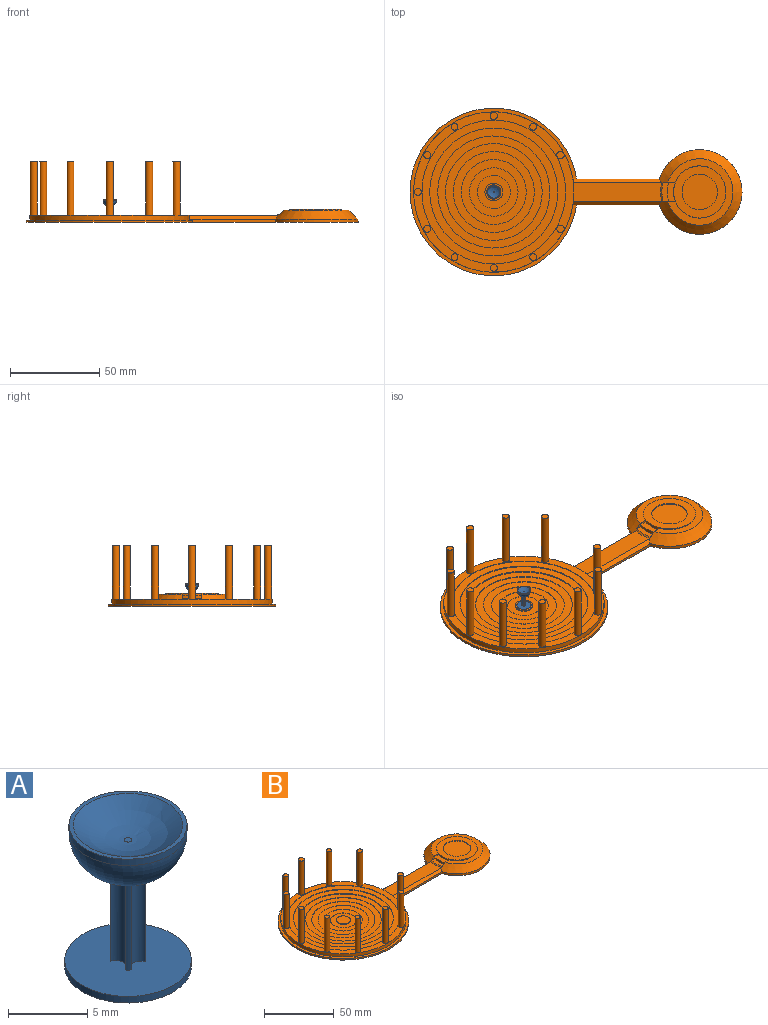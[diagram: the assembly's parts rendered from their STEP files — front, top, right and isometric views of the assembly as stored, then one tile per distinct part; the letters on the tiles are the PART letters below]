
ASSEMBLY  parts=2 mates=1
PART A: 20 faces, bbox 8x8x10.9 mm
  f0: plane 0.8x0.26mm, normal (0,0,-1), area 0.1mm2, adj f7,f17
  f1: plane 0.73x0.22mm, normal (0,0,-1), area 0.1mm2, adj f13,f17
  f2: plane 0.75x0.23mm, normal (0,0,-1), area 0.1mm2, adj f11,f17
  f3: cylinder r=4mm len=8mm, axis (0,0,-1), area 12.8mm2, adj f4,f5
  f4: plane 8x8mm, normal (0,0,1), area 48.8mm2, adj f3,f6,f7,f8,f9,f10,f11,f12
  f5: plane 8x8mm, normal (0,0,-1), area 50.3mm2, adj f3
  f6: cylinder r=1.12mm len=6.89mm, axis (0,0,-1), area 2.4mm2, adj f4,f7,f13,f17
  f7: cylinder r=0.71mm len=6.89mm, axis (0,0,-1), area 12.2mm2, adj f0,f4,f6,f8,f17
  f8: cylinder r=1.12mm len=6.89mm, axis (0,0,-1), area 2.6mm2, adj f4,f7,f9,f17
  f9: cylinder r=0.64mm len=6.89mm, axis (0,0,-1), area 11.2mm2, adj f4,f8,f10,f16,f17
  f10: cylinder r=1.12mm len=6.89mm, axis (0,0,-1), area 2.9mm2, adj f4,f9,f11,f17
  f11: cylinder r=0.68mm len=6.89mm, axis (0,0,-1), area 11.8mm2, adj f2,f4,f10,f12,f17
  f12: cylinder r=1.12mm len=6.89mm, axis (0,0,-1), area 2.6mm2, adj f4,f11,f13,f17
  f13: cylinder r=0.67mm len=6.89mm, axis (0,0,-1), area 11.7mm2, adj f1,f4,f6,f12,f17
  f14: cylinder r=3.73mm len=7.46mm, axis (0,0,-1), area 11.5mm2, adj f15,f17
  f15: plane 7.46x7.46mm, normal (0,0,1), area 6.3mm2, adj f14,f19
  f16: plane 0.66x0.18mm, normal (0,0,-1), area 0.1mm2, adj f9,f17
  f17: torus R=0.66mm, axis (0,0,1), area 78.6mm2, adj f0,f1,f2,f6,f7,f8,f9,f10
  f18: plane 0.48x0.48mm, normal (0,0,1), area 0.2mm2, adj f19
  f19: torus R=0.24mm, axis (0,0,-1), area 41.7mm2, adj f15,f18
PART B: 62 faces, bbox 186.4x94.1x34.1 mm
  f0: cylinder r=14.63mm len=29.27mm, axis (0,0,-1), area 62.7mm2, adj f2,f32,f33,f36,f59
  f1: plane 11.1x3.97mm, normal (0,0,1), area 34.9mm2, adj f2,f32,f34,f35
  f2: plane 6.98x2.59mm, normal (0,-1,0), area 8.5mm2, adj f0,f1,f33,f34,f35,f36
  f3: plane 48.53x1.58mm, normal (0,1,0), area 74.1mm2, adj f5,f25,f28,f29,f30,f31
  f4: plane 48.53x1.58mm, normal (0,-1,0), area 74.1mm2, adj f5,f25,f27,f29,f30,f31
  f5: cylinder r=45mm len=90mm, axis (0,0,-1), area 760.2mm2, adj f3,f4,f24,f26,f27,f28,f30
  f6: cylinder r=5mm len=10mm, axis (0,0,-1), area 16.8mm2, adj f7,f8
  f7: plane 10x10mm, normal (0,0,1), area 78.5mm2, adj f6
  f8: plane 18.46x18.46mm, normal (0,0,1), area 189.1mm2, adj f6,f9
  f9: cylinder r=9.23mm len=18.46mm, axis (0,0,-1), area 10.3mm2, adj f8,f10
  f10: plane 27.23x27.23mm, normal (0,0,1), area 314.9mm2, adj f9,f11
  f11: cylinder r=13.62mm len=27.23mm, axis (0,0,-1), area 17.4mm2, adj f10,f12
  f12: plane 36.41x36.41mm, normal (0,0,1), area 458.6mm2, adj f11,f13
  f13: cylinder r=18.2mm len=36.41mm, axis (0,0,-1), area 23.2mm2, adj f12,f14
  f14: plane 45.38x45.38mm, normal (0,0,1), area 576mm2, adj f13,f15
  f15: cylinder r=22.69mm len=45.38mm, axis (0,0,-1), area 29mm2, adj f14,f16
  f16: plane 54.32x54.32mm, normal (0,0,1), area 700.2mm2, adj f15,f17
  f17: cylinder r=27.16mm len=54.32mm, axis (0,0,-1), area 60.7mm2, adj f16,f18
  f18: plane 62.9x62.9mm, normal (0,0,1), area 790.3mm2, adj f17,f19
  f19: cylinder r=31.45mm len=62.9mm, axis (0,0,-1), area 110.4mm2, adj f18,f20
  f20: plane 71.81x71.81mm, normal (0,0,1), area 941.8mm2, adj f19,f21
  f21: cylinder r=35.9mm len=71.81mm, axis (0,0,-1), area 114.6mm2, adj f20,f22
  f22: plane 80.74x80.74mm, normal (0,0,1), area 1070.1mm2, adj f21,f23
  f23: cylinder r=40.37mm len=80.74mm, axis (0,0,-1), area 70.9mm2, adj f22,f24
  f24: plane 90x90mm, normal (0,0,1), area 1104.6mm2, adj f5,f23,f37,f39,f41,f43,f45,f47
  f25: plane 186.32x94.06mm, normal (0,0,-1), area 9381.5mm2, adj f3,f4,f29,f31
  f26: plane 49.55x10.56mm, normal (0,0,1), area 516.6mm2, adj f5,f27,f28,f34
  f27: plane 49.88x2.05mm, normal (0,-0.71,0.71), area 138.4mm2, adj f4,f5,f26,f31,f34
  f28: plane 49.87x2.04mm, normal (0,0.71,0.71), area 138.4mm2, adj f3,f5,f26,f31,f34
  f29: cylinder r=47.03mm len=94.06mm, axis (0,0,-1), area 356.7mm2, adj f3,f4,f25,f30
  f30: plane 94.06x93.5mm, normal (0,0,1), area 557.8mm2, adj f3,f4,f5,f29
  f31: cylinder r=23.75mm len=47.5mm, axis (0,0,-1), area 239.1mm2, adj f3,f4,f25,f27,f28,f34
  f32: plane 6.98x2.59mm, normal (0,1,0), area 8.5mm2, adj f0,f1,f33,f34,f35,f36
  f33: plane 37.34x36.5mm, normal (0,0,1), area 376.7mm2, adj f0,f2,f32,f34
  f34: cone r=18.67mm half-angle=45deg, axis (0,0,-1), area 885.1mm2, adj f1,f2,f26,f27,f28,f31,f32,f33
  f35: cylinder r=18.11mm len=11.1mm, axis (0,0,-1), area 17.5mm2, adj f1,f2,f32,f36
  f36: plane 11.1x4.57mm, normal (0,0,1), area 39.4mm2, adj f0,f2,f32,f35
  f37: cylinder r=1.99mm len=30mm, axis (0,0,-1), area 375.8mm2, adj f24,f38
  f38: plane 3.99x3.99mm, normal (0,0,1), area 12.5mm2, adj f37
  f39: cylinder r=1.98mm len=30mm, axis (0,0,-1), area 373.5mm2, adj f24,f40
  f40: plane 3.96x3.96mm, normal (0,0,1), area 12.3mm2, adj f39
  f41: cylinder r=2.08mm len=30mm, axis (0,0,-1), area 392.1mm2, adj f24,f42
  f42: plane 4.16x4.16mm, normal (0,0,1), area 13.6mm2, adj f41
  f43: cylinder r=1.96mm len=30mm, axis (0,0,-1), area 368.6mm2, adj f24,f44
  f44: plane 3.91x3.91mm, normal (0,0,1), area 12mm2, adj f43
  f45: cylinder r=1.92mm len=30mm, axis (0,0,-1), area 362.7mm2, adj f24,f46
  f46: plane 3.85x3.85mm, normal (0,0,1), area 11.6mm2, adj f45
  f47: cylinder r=1.97mm len=30mm, axis (0,0,-1), area 372.2mm2, adj f24,f48
  f48: plane 3.95x3.95mm, normal (0,0,1), area 12.2mm2, adj f47
  f49: cylinder r=2.09mm len=30mm, axis (0,0,-1), area 393.1mm2, adj f24,f50
  f50: plane 4.17x4.17mm, normal (0,0,1), area 13.7mm2, adj f49
  f51: cylinder r=1.96mm len=30mm, axis (0,0,-1), area 368.6mm2, adj f24,f52
  f52: plane 3.91x3.91mm, normal (0,0,1), area 12mm2, adj f51
  f53: cylinder r=1.92mm len=30mm, axis (0,0,-1), area 362.7mm2, adj f24,f54
  f54: plane 3.85x3.85mm, normal (0,0,1), area 11.6mm2, adj f53
  f55: cylinder r=1.97mm len=30mm, axis (0,0,-1), area 372.2mm2, adj f24,f56
  f56: plane 3.95x3.95mm, normal (0,0,1), area 12.2mm2, adj f55
  f57: cylinder r=2.09mm len=30mm, axis (0,0,-1), area 393.1mm2, adj f24,f58
  f58: plane 4.17x4.17mm, normal (0,0,1), area 13.7mm2, adj f57
  f59: plane 29.27x29.27mm, normal (0,0,1), area 363.2mm2, adj f0,f61
  f60: plane 19.86x19.86mm, normal (0,0,1), area 309.7mm2, adj f61
  f61: cylinder r=9.93mm len=19.86mm, axis (0,0,1), area 38mm2, adj f59,f60
PLACE A t=(-47,-47.7,8.38)mm
PLACE B t=(-10.06,2.25,6.62)mm
MATE parallel A.f3 <-> B.f5  axis (0,0,-1) through (-47,-47.7,8.38)mm
